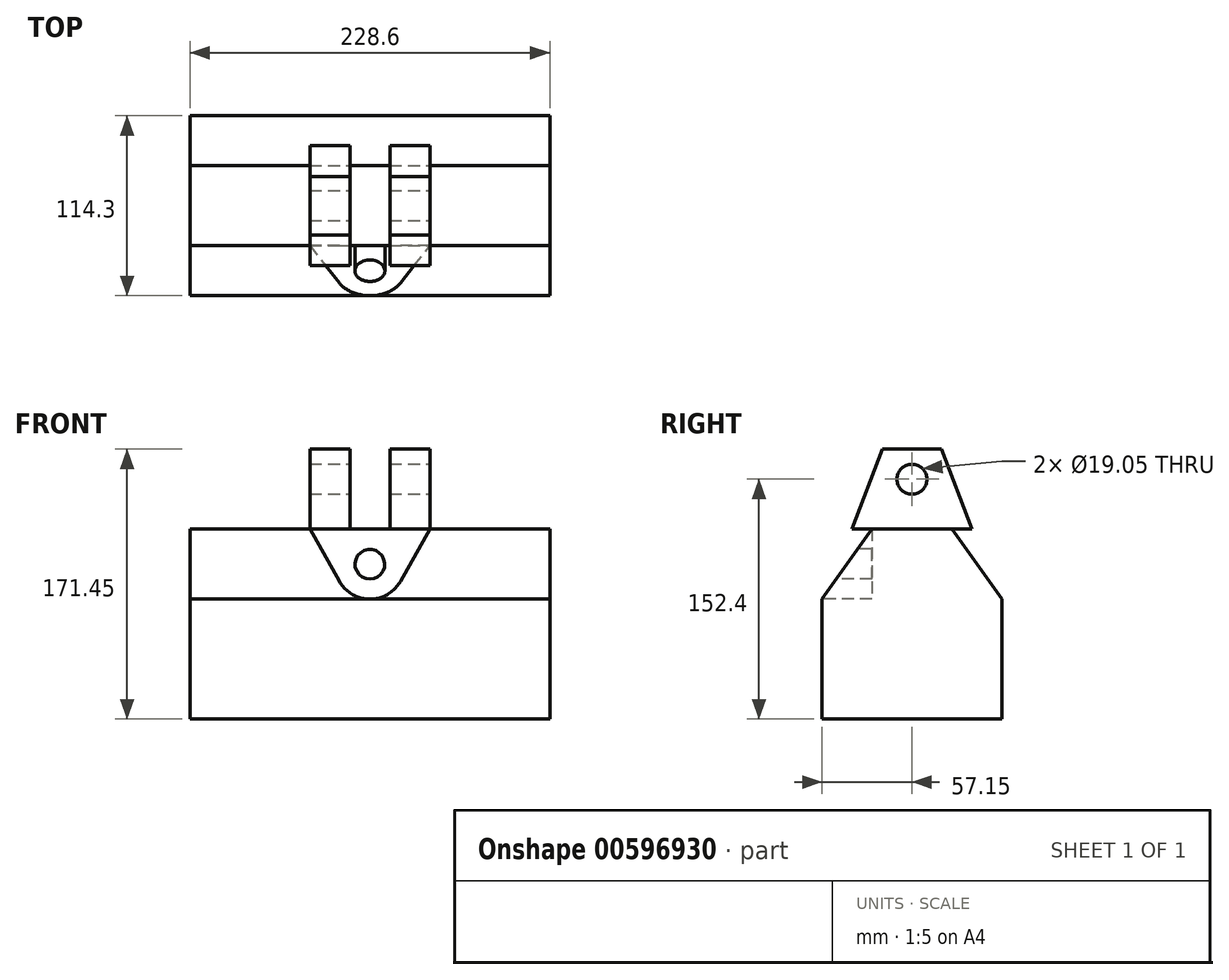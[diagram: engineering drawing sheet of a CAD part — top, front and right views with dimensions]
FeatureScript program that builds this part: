
annotation { "Feature Type Name" : "Feature", "Feature Type Description" : "" }
export const myFeature = defineFeature(function(context is Context, id is Id, definition is map)
    precondition{}
    {
        {
            var Q0;
            Q0=qCreatedBy(makeId("Top.planeOp"),FACE);
            var sketch = newSketch(context, id + "F0", { "sketchPlane" : qUnion([Q0])});
            skLineSegment(sketch, "E0.bottom", {"start": v(0, 0) * mm, "end": v(-228.6, 0) * mm});
            skLineSegment(sketch, "E0.top", {"start": v(0, 114.3) * mm, "end": v(-228.6, 114.3) * mm});
            skLineSegment(sketch, "E0.left", {"start": v(0, 0) * mm, "end": v(0, 114.3) * mm});
            skLineSegment(sketch, "E0.right", {"start": v(-228.6, 0) * mm, "end": v(-228.6, 114.3) * mm});
            skSolve(sketch);
        }
        {
            var Q0;
            Q0 = qSketchRegion(id + "F0", true);
            extrude(context, id + "F1", {"entities" : qUnion([Q0]), "depth" : 120.65 * mm, "offsetDistance" : 25.4 * mm});
        }
        {
            var Q0;
            Q0=makeQuery(id+"F1.opExtrude","CAP_EDGE",EDGE,{"disambiguationData":[OSD([sQuery(id+"F0.wireOp",EDGE,"E0.top")])],"isStart":false});
            cPoint(context, id + "F2", {"entities" : qUnion([Q0]), "parameter" : 0.5});
        }
        {
            var Q0;
            Q0=makeQuery(id+"F1.opExtrude","CAP_EDGE",EDGE,{"disambiguationData":[OSD([sQuery(id+"F0.wireOp",EDGE,"E0.bottom")])],"isStart":false});
            cPoint(context, id + "F3", {"entities" : qUnion([Q0]), "parameter" : 0.5});
        }
        {
            var Q0;
            Q0=makeQuery(id+"F1.opExtrude","CAP_EDGE",EDGE,{"disambiguationData":[OSD([sQuery(id+"F0.wireOp",EDGE,"E0.bottom")])],"isStart":true});
            cPoint(context, id + "F4", {"entities" : qUnion([Q0]), "parameter" : 0.5});
        }
        {
            var Q0;
            Q0 = qCreatedBy(id + "F2" ,VERTEX);
            var Q1;
            Q1 = qCreatedBy(id + "F3" ,VERTEX);
            var Q2;
            Q2 = qCreatedBy(id + "F4" ,VERTEX);
            cPlane(context, id + "F5", {"entities" : qUnion([Q0, Q1, Q2]), "cplaneType" : CPlaneType.THREE_POINT, "offset" : 25.4 * mm, "width" : 152.4 * mm, "height" : 152.4 * mm});
        }
        {
            var Q0;
            Q0=qCreatedBy(id+"F5.planeOp",FACE);
            var sketch = newSketch(context, id + "F6", { "sketchPlane" : qUnion([Q0])});
            skLineSegment(sketch, "E1", {"start": v(-95.25, 120.65) * mm, "end": v(-19.05, 120.65) * mm});
            skLineSegment(sketch, "E2", {"start": v(-19.05, 120.65) * mm, "end": v(-38.55, 171.45) * mm});
            skLineSegment(sketch, "E3", {"start": v(-38.55, 171.45) * mm, "end": v(-75.75, 171.45) * mm});
            skLineSegment(sketch, "E4", {"start": v(-75.75, 171.45) * mm, "end": v(-95.25, 120.65) * mm});
            skCircle(sketch, "E5", {"center": v(-57.15, 152.4) * mm, "radius": 9.53 * mm});
            skPoint(sketch, "E6", {"position": v(-57.15, 120.65) * mm});
            skSolve(sketch);
        }
        {
            var Q0;
            Q0 = qSketchRegion(id + "F6", true);
            extrude(context, id + "F7", {"entities" : qUnion([Q0]), "operationType" : NewBodyOperationType.ADD, "endBound" : BoundingType.SYMMETRIC, "depth" : 76.2 * mm, "offsetDistance" : 25.4 * mm});
        }
        {
            var Q0;
            Q0 = qSketchRegion(id + "F6", true);
            extrude(context, id + "F8", {"entities" : qUnion([Q0]), "operationType" : NewBodyOperationType.REMOVE, "endBound" : BoundingType.SYMMETRIC, "oppositeDirection" : true, "depth" : 25.4 * mm, "offsetDistance" : 25.4 * mm});
        }
        {
            var Q0;
            Q0=makeQuery(id+"F1.opExtrude","SWEPT_FACE",FACE,{"disambiguationData":[OSD([sQuery(id+"F0.wireOp",EDGE,"E0.left")])]});
            var sketch = newSketch(context, id + "F9", { "sketchPlane" : qUnion([Q0])});
            skLineSegment(sketch, "E7", {"start": v(0, 120.65) * mm, "end": v(0, 76.2) * mm});
            skLineSegment(sketch, "E8", {"start": v(0, 76.2) * mm, "end": v(31.75, 120.65) * mm});
            skLineSegment(sketch, "E9", {"start": v(31.75, 120.65) * mm, "end": v(0, 120.65) * mm});
            skLineSegment(sketch, "E10", {"start": v(82.55, 120.65) * mm, "end": v(114.3, 120.65) * mm});
            skLineSegment(sketch, "E11", {"start": v(114.3, 120.65) * mm, "end": v(114.3, 76.2) * mm});
            skLineSegment(sketch, "E12", {"start": v(114.3, 76.2) * mm, "end": v(82.55, 120.65) * mm});
            skSolve(sketch);
        }
        {
            var Q0;
            Q0 = qSketchRegion(id + "F9", true);
            extrude(context, id + "F10", {"entities" : qUnion([Q0]), "operationType" : NewBodyOperationType.REMOVE, "endBound" : BoundingType.UP_TO_NEXT, "oppositeDirection" : true, "depth" : 25.4 * mm, "offsetDistance" : 25.4 * mm});
        }
        {
            var Q0;
            Q0=makeQuery(id+"F1.opExtrude","SWEPT_FACE",FACE,{"disambiguationData":[OSD([sQuery(id+"F0.wireOp",EDGE,"E0.bottom")])]});
            var sketch = newSketch(context, id + "F11", { "sketchPlane" : qUnion([Q0])});
            skCircle(sketch, "E13", {"center": v(-114.3, 98.43) * mm, "radius": 9.53 * mm});
            skLineSegment(sketch, "E14", {"start": v(-114.3, 76.2) * mm, "end": v(-114.3, 120.65) * mm, "construction": true});
            skArc(sketch, "E15", {"start": v(-133.65, 87.49) * mm, "mid": v(-114.3, 76.2) * mm, "end": v(-94.95, 87.49) * mm});
            skLineSegment(sketch, "E16", {"start": v(-133.65, 87.49) * mm, "end": v(-152.4, 120.65) * mm});
            skLineSegment(sketch, "E17", {"start": v(-152.4, 120.65) * mm, "end": v(-76.2, 120.65) * mm});
            skLineSegment(sketch, "E18", {"start": v(-76.2, 120.65) * mm, "end": v(-94.95, 87.49) * mm});
            skSolve(sketch);
        }
        {
            var Q0;
            Q0 = qSketchRegion(id + "F11", true);
            extrude(context, id + "F12", {"entities" : qUnion([Q0]), "operationType" : NewBodyOperationType.REMOVE, "oppositeDirection" : true, "depth" : 31.75 * mm, "offsetDistance" : 25.4 * mm});
        }
        {
            var Q0;
            Q0=makeQuery(id+"F1.opExtrude","CAP_EDGE",EDGE,{"disambiguationData":[OSD([sQuery(id+"F0.wireOp",EDGE,"E0.left")])],"isStart":false});
            cPoint(context, id + "F13", {"entities" : qUnion([Q0]), "parameter" : 0.5});
        }
        {
            var Q0;
            Q0=makeQuery(id+"F1.opExtrude","CAP_EDGE",EDGE,{"disambiguationData":[OSD([sQuery(id+"F0.wireOp",EDGE,"E0.left")])],"isStart":true});
            cPoint(context, id + "F14", {"entities" : qUnion([Q0]), "parameter" : 0.5});
        }
        {
            var Q0;
            Q0=makeQuery(id+"F1.opExtrude","CAP_EDGE",EDGE,{"disambiguationData":[OSD([sQuery(id+"F0.wireOp",EDGE,"E0.right")])],"isStart":true});
            cPoint(context, id + "F15", {"entities" : qUnion([Q0]), "parameter" : 0.5});
        }
        {
            var Q0;
            Q0 = qCreatedBy(id + "F13" ,VERTEX);
            var Q1;
            Q1 = qCreatedBy(id + "F14" ,VERTEX);
            var Q2;
            Q2 = qCreatedBy(id + "F15" ,VERTEX);
            cPlane(context, id + "F16", {"entities" : qUnion([Q0, Q1, Q2]), "cplaneType" : CPlaneType.THREE_POINT, "offset" : 25.4 * mm, "width" : 152.4 * mm, "height" : 152.4 * mm});
        }
    });
